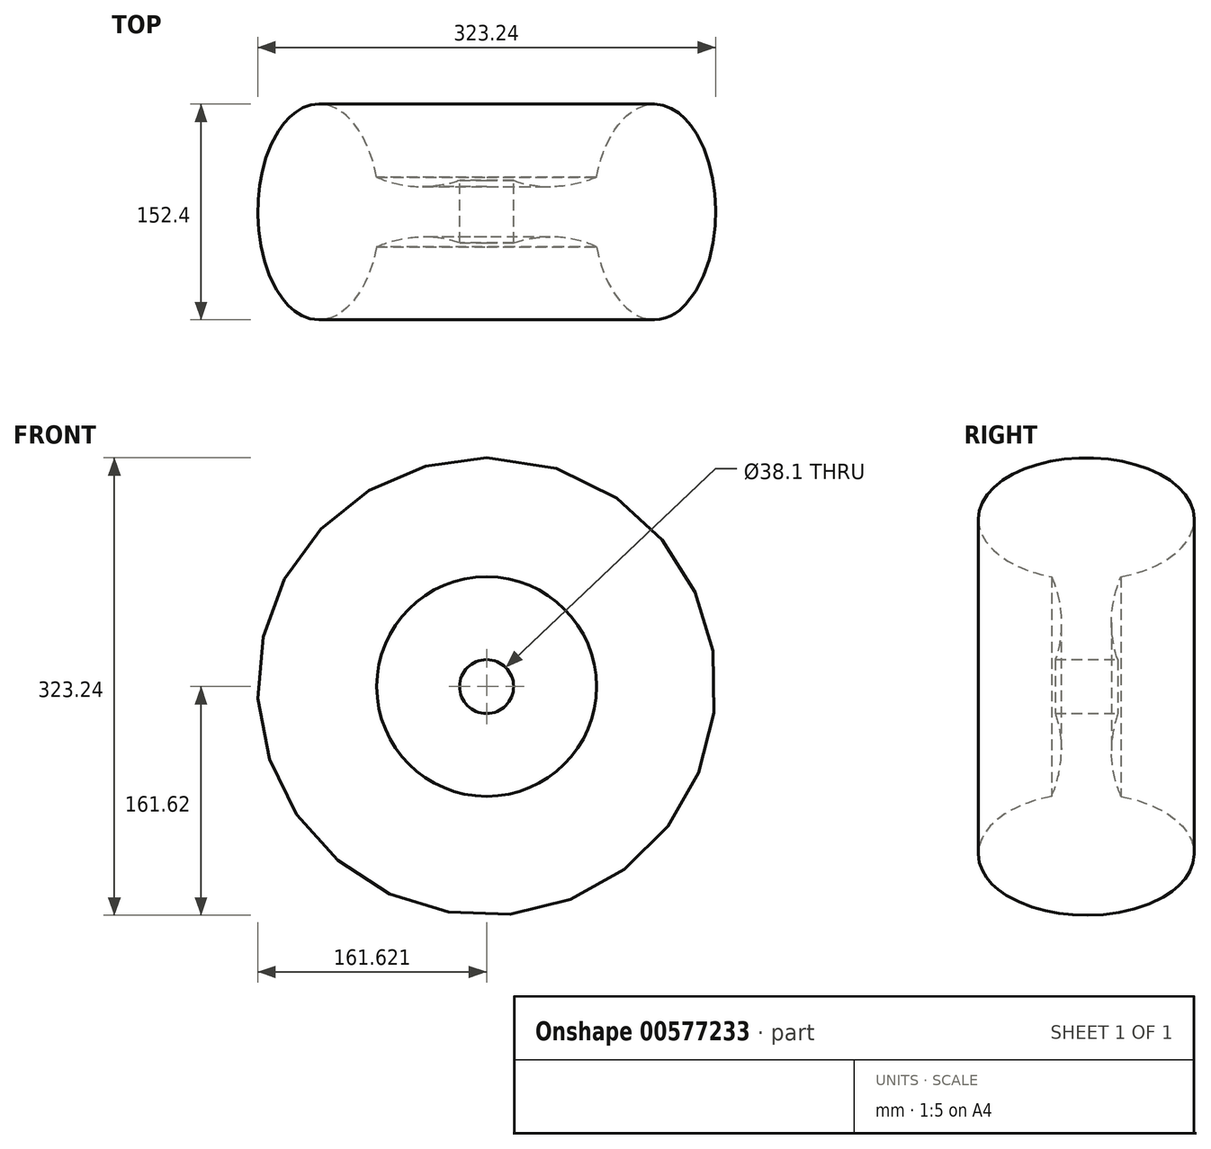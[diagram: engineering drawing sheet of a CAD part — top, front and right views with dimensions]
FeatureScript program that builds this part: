
annotation { "Feature Type Name" : "Feature", "Feature Type Description" : "" }
export const myFeature = defineFeature(function(context is Context, id is Id, definition is map)
    precondition{}
    {
        {
            var Q0;
            Q0=qCreatedBy(makeId("Top.planeOp"),FACE);
            var sketch = newSketch(context, id + "F0", { "sketchPlane" : qUnion([Q0])});
            skEllipticalArc(sketch, "E0", {});
            skArc(sketch, "E1", {"start": v(-16.36, 24.57) * mm, "mid": v(12.67, 17.88) * mm, "end": v(42.15, 22.2) * mm});
            skArc(sketch, "E2.MirrorCS", {"start": v(-16.36, -24.57) * mm, "mid": v(12.64, -17.7) * mm, "end": v(42.15, -21.84) * mm});
            skLineSegment(sketch, "E3", {"start": v(42.15, 22.2) * mm, "end": v(42.15, -21.84) * mm});
            skLineSegment(sketch, "E4", {"start": v(37.42, 22.2) * mm, "end": v(38.26, 22.2) * mm});
            skLineSegment(sketch, "E5", {"start": v(61.2, 22.2) * mm, "end": v(61.2, -85.72) * mm});
            const initialGuessF0  = {"E0": [-0.057237166849633106, 0, 0, -1, 0.0762, 0.04318, 1.8991518800453906, 1.2424407735444023]};
            skSetInitialGuess(sketch, initialGuessF0);
            skSolve(sketch);
        }
        {
            var Q0;
            Q0=makeQuery(id+"F0.imprint","IMPRINT",FACE,{"disambiguationData":[TD([[makeQuery(id+"F0.imprint","IMPRINT",EDGE,{"derivedFrom":sQuery(id+"F0.wireOp",EDGE,"E0")}),1.0]])]});
            var Q1;
            Q1=sQuery(id+"F0.wireOp",EDGE,"E5");
            revolve(context, id + "F1", {"entities" : qUnion([Q0]), "axis" : qUnion([Q1]), "revolveType" : RevolveType.FULL});
        }
    });
